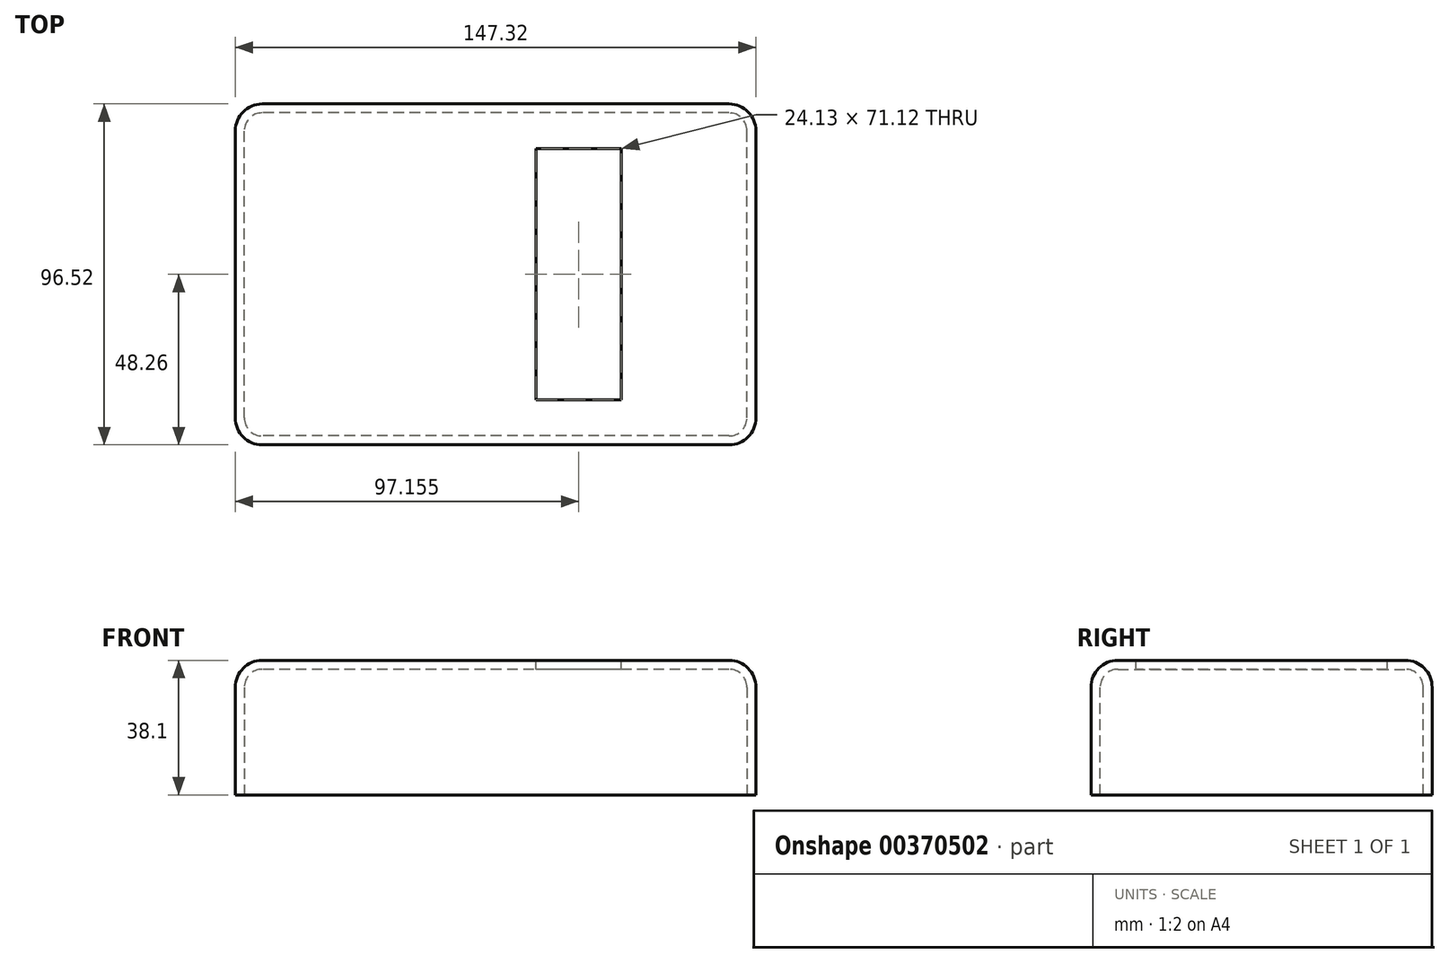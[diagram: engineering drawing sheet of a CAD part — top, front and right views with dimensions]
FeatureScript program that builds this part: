
annotation { "Feature Type Name" : "Feature", "Feature Type Description" : "" }
export const myFeature = defineFeature(function(context is Context, id is Id, definition is map)
    precondition{}
    {
        {
            var Q0;
            Q0=qCreatedBy(makeId("Front.planeOp"),FACE);
            var sketch = newSketch(context, id + "F0", { "sketchPlane" : qUnion([Q0])});
            skLineSegment(sketch, "E0.bottom", {"start": v(66.04, 19.05) * mm, "end": v(-66.04, 19.05) * mm});
            skLineSegment(sketch, "E0.top", {"start": v(73.66, -19.05) * mm, "end": v(-73.66, -19.05) * mm});
            skLineSegment(sketch, "E0.left", {"start": v(73.66, 11.43) * mm, "end": v(73.66, -19.05) * mm});
            skLineSegment(sketch, "E0.right", {"start": v(-73.66, 11.43) * mm, "end": v(-73.66, -19.05) * mm});
            skPoint(sketch, "E0.middle", {"position": v(0, 0) * mm});
            skPoint(sketch, "E1.visualSharp", {"position": v(-73.66, 19.05) * mm});
            skArc(sketch, "E1.filletArc", {"start": v(-66.04, 19.05) * mm, "mid": v(-71.43, 16.82) * mm, "end": v(-73.66, 11.43) * mm});
            skPoint(sketch, "E2.visualSharp", {"position": v(73.66, 19.05) * mm});
            skArc(sketch, "E2.filletArc", {"start": v(73.66, 11.43) * mm, "mid": v(71.43, 16.82) * mm, "end": v(66.04, 19.05) * mm});
            skSolve(sketch);
        }
        {
            var Q0;
            Q0 = qSketchRegion(id + "F0", true);
            extrude(context, id + "F1", {"entities" : qUnion([Q0]), "endBound" : BoundingType.SYMMETRIC, "depth" : 96.52 * mm});
        }
        {
            var Q0;
            Q0=makeQuery(id+"F1.opExtrude","SWEPT_EDGE",EDGE,{"disambiguationData":[OSD([sQuery(id+"F0.wireOp",EDGE,"E0.bottom"),sQuery(id+"F0.wireOp",EDGE,"E2.filletArc")])]});
            var Q1;
            Q1=makeQuery(id+"F1.opExtrude","SWEPT_EDGE",EDGE,{"disambiguationData":[OSD([sQuery(id+"F0.wireOp",EDGE,"E0.bottom"),sQuery(id+"F0.wireOp",EDGE,"E1.filletArc")])]});
            var Q2;
            Q2=makeQuery(id+"F1.opExtrude","CAP_EDGE",EDGE,{"disambiguationData":[OSD([sQuery(id+"F0.wireOp",EDGE,"E2.filletArc")])],"isStart":true});
            fillet(context, id + "F2", {"entities" : qUnion([Q0, Q1, Q2]), "radius" : 7.62 * mm, "tangentPropagation" : true, "allowEdgeOverflow" : false});
        }
        {
            var Q0;
            Q0=makeQuery(id+"F1.opExtrude","SWEPT_EDGE",EDGE,{"disambiguationData":[OSD([sQuery(id+"F0.wireOp",EDGE,"E0.bottom"),sQuery(id+"F0.wireOp",EDGE,"E2.filletArc")])]});
            var Q1;
            Q1=makeQuery(id+"F1.opExtrude","CAP_EDGE",EDGE,{"disambiguationData":[OSD([sQuery(id+"F0.wireOp",EDGE,"E2.filletArc")])],"isStart":false});
            fillet(context, id + "F3", {"entities" : qUnion([Q0, Q1]), "radius" : 7.62 * mm, "tangentPropagation" : true, "allowEdgeOverflow" : false});
        }
        {
            var Q0;
            Q0=makeQuery(id+"F1.opExtrude","SWEPT_FACE",FACE,{"disambiguationData":[OSD([sQuery(id+"F0.wireOp",EDGE,"E0.top")])]});
            shell(context, id + "F4", {"entities" : qUnion([Q0]), "thickness" : 2.54 * mm});
        }
        {
            var Q0;
            Q0=makeQuery(id+"F1.opExtrude","SWEPT_FACE",FACE,{"disambiguationData":[OSD([sQuery(id+"F0.wireOp",EDGE,"E0.bottom")])]});
            var sketch = newSketch(context, id + "F5", { "sketchPlane" : qUnion([Q0])});
            skLineSegment(sketch, "E3.bottom", {"start": v(35.56, 35.56) * mm, "end": v(11.43, 35.56) * mm});
            skLineSegment(sketch, "E3.top", {"start": v(35.56, -35.56) * mm, "end": v(11.43, -35.56) * mm});
            skLineSegment(sketch, "E3.left", {"start": v(35.56, 35.56) * mm, "end": v(35.56, -35.56) * mm});
            skLineSegment(sketch, "E3.right", {"start": v(11.43, 35.56) * mm, "end": v(11.43, -35.56) * mm});
            skSolve(sketch);
        }
        {
            var Q0;
            Q0=makeQuery(id+"F5.imprint","IMPRINT",FACE,{"disambiguationData":[TD([[makeQuery(id+"F5.imprint","IMPRINT",EDGE,{"derivedFrom":sQuery(id+"F5.wireOp",EDGE,"E3.bottom")}),1.0]])]});
            extrude(context, id + "F6", {"entities" : qUnion([Q0]), "operationType" : NewBodyOperationType.REMOVE, "endBound" : BoundingType.UP_TO_NEXT, "oppositeDirection" : true, "depth" : 25.4 * mm});
        }
    });
